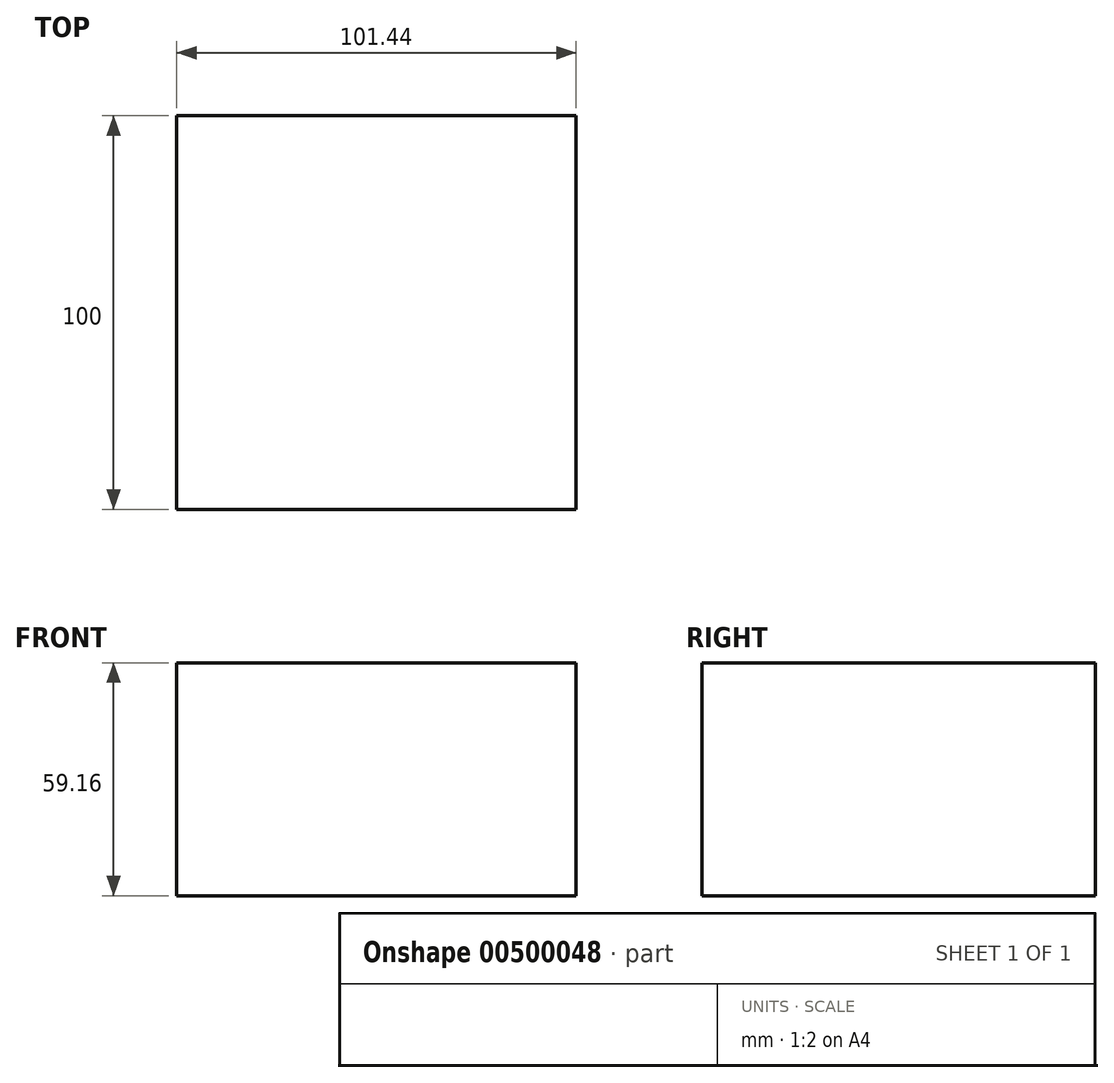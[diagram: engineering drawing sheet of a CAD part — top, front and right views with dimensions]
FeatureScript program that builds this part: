
annotation { "Feature Type Name" : "Feature", "Feature Type Description" : "" }
export const myFeature = defineFeature(function(context is Context, id is Id, definition is map)
    precondition{}
    {
        {
            var Q0;
            Q0=qCreatedBy(makeId("Front.planeOp"),FACE);
            var sketch = newSketch(context, id + "F0", { "sketchPlane" : qUnion([Q0])});
            skLineSegment(sketch, "E0.bottom", {"start": v(50.72, 29.58) * mm, "end": v(-50.72, 29.58) * mm});
            skLineSegment(sketch, "E0.top", {"start": v(50.72, -29.58) * mm, "end": v(-50.72, -29.58) * mm});
            skLineSegment(sketch, "E0.left", {"start": v(50.72, 29.58) * mm, "end": v(50.72, -29.58) * mm});
            skLineSegment(sketch, "E0.right", {"start": v(-50.72, 29.58) * mm, "end": v(-50.72, -29.58) * mm});
            skPoint(sketch, "E0.middle", {"position": v(0, 0) * mm});
            skSolve(sketch);
        }
        {
            var Q0;
            Q0 = qSketchRegion(id + "F0", true);
            extrude(context, id + "F1", {"entities" : qUnion([Q0]), "endBound" : BoundingType.SYMMETRIC, "depth" : 100 * mm});
        }
    });
